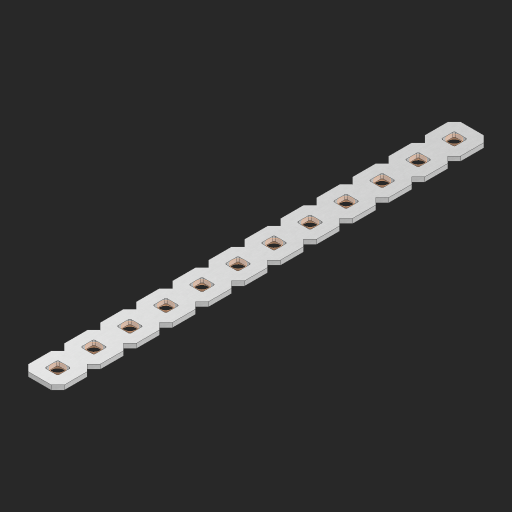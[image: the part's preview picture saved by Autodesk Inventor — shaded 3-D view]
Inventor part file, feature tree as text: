
AUTODESK INVENTOR PART (.ipt)
format: ipt  version: 2023 (Build 270158000, 158)  size: 395,264 bytes
history: native  units: in
note: dims shown in document units (in); Inventor stores cm internally (conversion verified against a paired STEP export)
features: other x13, extrude x11, sketch x2, pattern_linear x1
ambient origin geometry x8: Origin, YZ Plane, XZ Plane, XY Plane, X Axis, Y Axis, Z Axis, Center Point
bodies: Solid1 (feature_tree), Body (feature_tree)
feature tree (27):
  pattern_linear  "Rectangular Pattern1"  Spacing1=0.09in  [1 undecoded]
  sketch  "Sketch1"  dims[d1=0.5in]
  sketch  "Sketch2"  dims[d2=0.182in d3=0.09in d4=0.09in d5=0.09in d6=0.09in d7=0.09in d8=0.09in d9=0.09in d10=0.09in d11=0.02in d13=0.0in d14=0.172in d15=0.0625in d16=0.0in d19=0.5in d22=0.5in]
  other  "Srf1"
  other  "Srf126"
  other  "Srf127"
  other  "Srf128"
  other  "Srf129"
  other  "Srf130"
  other  "Srf131"
  other  "Srf250"
  other  "Srf251"
  other  "Srf252"
  other  "Srf253"
  other  "Srf254"
  other  "Circle"
  extrude  "ExtrusionSrf126"  Depth=0.09in
  extrude  "ExtrusionSrf127"  Depth=0.09in
  extrude  "ExtrusionSrf128"  Depth=0.09in
  extrude  "ExtrusionSrf129"  Depth=0.09in
  extrude  "ExtrusionSrf130"  Depth=0.09in
  extrude  "ExtrusionSrf131"  Depth=0.09in
  extrude  "ExtrusionSrf250"  Depth=0.09in
  extrude  "ExtrusionSrf251"  Depth=0.02in
  extrude  "ExtrusionSrf252"  TaperAngle=0.0deg  [1 undecoded]
  extrude  "ExtrusionSrf253"  Depth=0.5in
  extrude  "ExtrusionSrf254"  Depth=0.0625in TaperAngle=0.0deg
note: 2 required parameter values undecoded (feature->parameter linkage not recoverable at this tier; creation-order binding heuristic only, values carry confidence <= 0.55)
